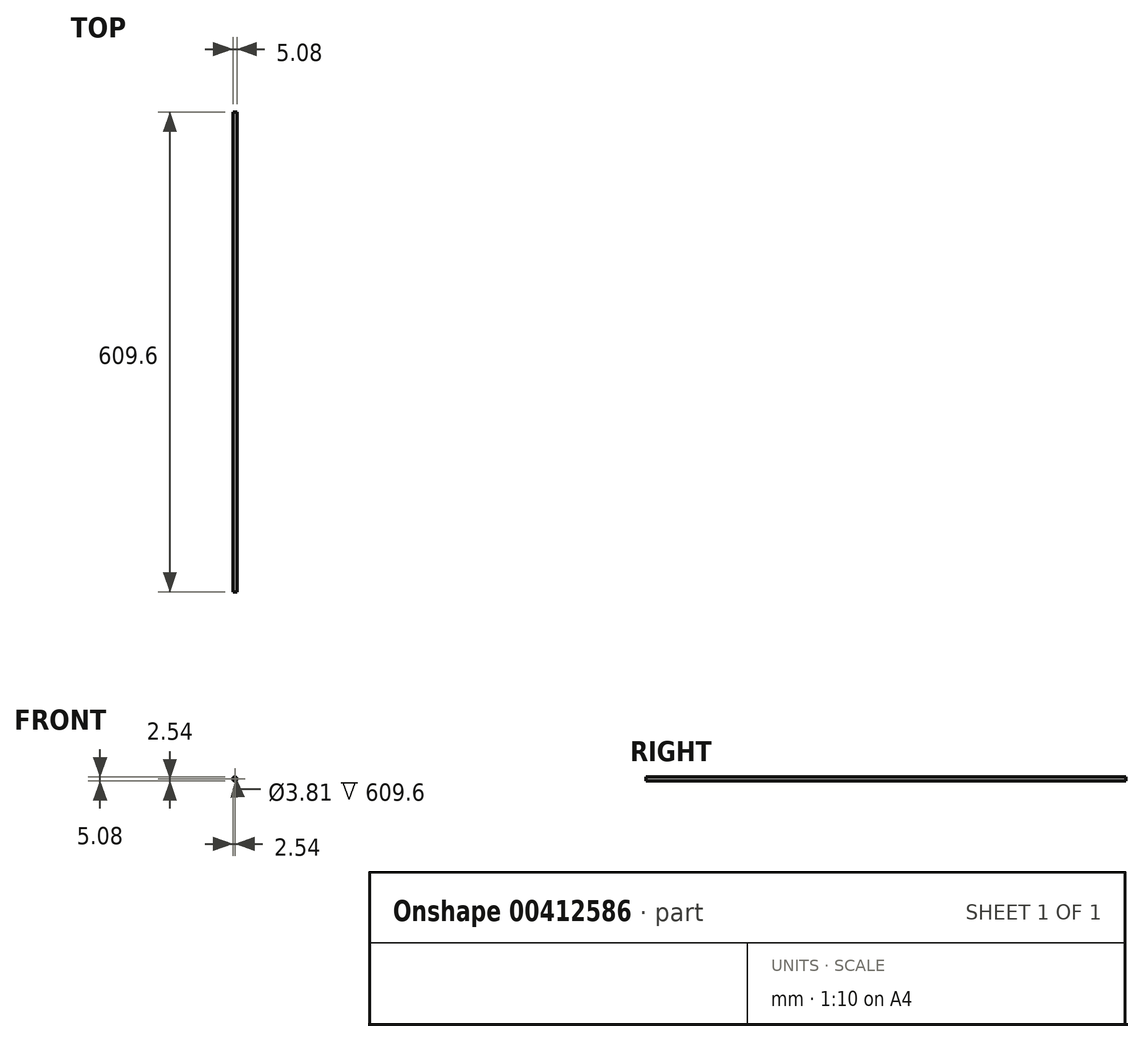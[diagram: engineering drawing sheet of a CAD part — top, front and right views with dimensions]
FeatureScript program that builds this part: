
annotation { "Feature Type Name" : "Feature", "Feature Type Description" : "" }
export const myFeature = defineFeature(function(context is Context, id is Id, definition is map)
    precondition{}
    {
        {
            var Q0;
            Q0=qCreatedBy(makeId("Front.planeOp"),FACE);
            var sketch = newSketch(context, id + "F0", { "sketchPlane" : qUnion([Q0])});
            skCircle(sketch, "E0", {"center": v(0, 0) * mm, "radius": 2.54 * mm});
            skCircle(sketch, "E1", {"center": v(0, 0) * mm, "radius": 1.9 * mm});
            skSolve(sketch);
        }
        {
            var Q0;
            Q0=makeQuery(id+"F0.imprint","IMPRINT",FACE,{"disambiguationData":[TD([[makeQuery(id+"F0.imprint","IMPRINT",EDGE,{"derivedFrom":sQuery(id+"F0.wireOp",EDGE,"E0")}),1.0]])]});
            extrude(context, id + "F1", {"entities" : qUnion([Q0]), "depth" : 609.6 * mm});
        }
    });
